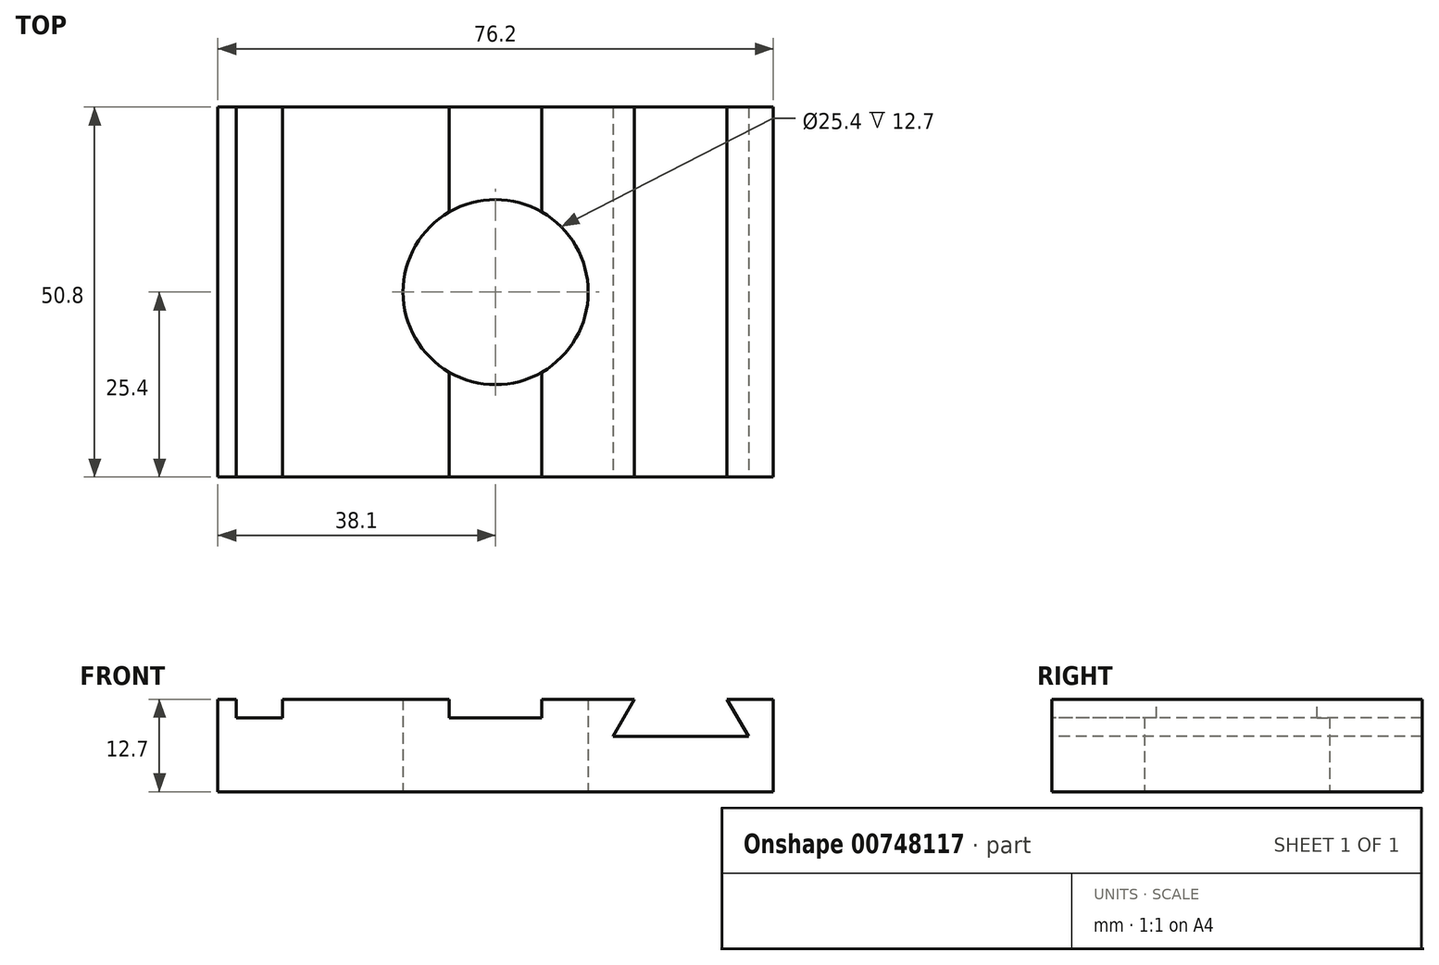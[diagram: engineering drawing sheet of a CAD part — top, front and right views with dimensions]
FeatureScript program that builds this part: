
annotation { "Feature Type Name" : "Feature", "Feature Type Description" : "" }
export const myFeature = defineFeature(function(context is Context, id is Id, definition is map)
    precondition{}
    {
        {
            var Q0;
            Q0=qCreatedBy(makeId("Top.planeOp"),FACE);
            var sketch = newSketch(context, id + "F0", { "sketchPlane" : qUnion([Q0])});
            skLineSegment(sketch, "E0.bottom", {"start": v(38.1, -25.4) * mm, "end": v(-38.1, -25.4) * mm});
            skLineSegment(sketch, "E0.top", {"start": v(38.1, 25.4) * mm, "end": v(-38.1, 25.4) * mm});
            skLineSegment(sketch, "E0.left", {"start": v(38.1, -25.4) * mm, "end": v(38.1, 25.4) * mm});
            skLineSegment(sketch, "E0.right", {"start": v(-38.1, -25.4) * mm, "end": v(-38.1, 25.4) * mm});
            skPoint(sketch, "E0.middle", {"position": v(0, 0) * mm});
            skCircle(sketch, "E1", {"center": v(0, 0) * mm, "radius": 12.7 * mm});
            skSolve(sketch);
        }
        {
            var Q0;
            Q0=makeQuery(id+"F0.imprint","IMPRINT",FACE,{"disambiguationData":[TD([[makeQuery(id+"F0.imprint","IMPRINT",EDGE,{"derivedFrom":sQuery(id+"F0.wireOp",EDGE,"E0.bottom")}),-1.0]])]});
            extrude(context, id + "F1", {"entities" : qUnion([Q0]), "depth" : 12.7 * mm, "offsetDistance" : 25.4 * mm});
        }
        {
            var Q0;
            Q0=makeQuery(id+"F1.opExtrude","CAP_FACE",FACE,{"disambiguationData":[OSD([sQuery(id+"F0.wireOp",EDGE,"E0.bottom"),sQuery(id+"F0.wireOp",EDGE,"E0.top"),sQuery(id+"F0.wireOp",EDGE,"E0.left"),sQuery(id+"F0.wireOp",EDGE,"E0.right"),sQuery(id+"F0.wireOp",EDGE,"E1")])],"isStart":false});
            var sketch = newSketch(context, id + "F2", { "sketchPlane" : qUnion([Q0])});
            skLineSegment(sketch, "E2.bottom", {"start": v(-35.56, 25.4) * mm, "end": v(-29.21, 25.4) * mm});
            skLineSegment(sketch, "E2.top", {"start": v(-35.56, -25.4) * mm, "end": v(-29.21, -25.4) * mm});
            skLineSegment(sketch, "E2.left", {"start": v(-35.56, 25.4) * mm, "end": v(-35.56, -25.4) * mm});
            skLineSegment(sketch, "E2.right", {"start": v(-29.21, 25.4) * mm, "end": v(-29.21, -25.4) * mm});
            skLineSegment(sketch, "E3", {"start": v(-6.35, 25.4) * mm, "end": v(-6.35, -25.4) * mm});
            skLineSegment(sketch, "E4", {"start": v(-6.35, -25.4) * mm, "end": v(6.35, -25.4) * mm});
            skLineSegment(sketch, "E5", {"start": v(6.35, -25.4) * mm, "end": v(6.35, 25.4) * mm});
            skLineSegment(sketch, "E6", {"start": v(6.35, 25.4) * mm, "end": v(-6.35, 25.4) * mm});
            skPoint(sketch, "E7", {"position": v(0, 0) * mm});
            skPoint(sketch, "E8", {"position": v(0, 25.4) * mm});
            skLineSegment(sketch, "E9", {"start": v(0, 25.4) * mm, "end": v(0, -25.4) * mm, "construction": true});
            skSolve(sketch);
        }
        {
            var Q0;
            Q0=makeQuery(id+"F2.imprint","IMPRINT",FACE,{"disambiguationData":[TD([[makeQuery(id+"F2.imprint","IMPRINT",EDGE,{"derivedFrom":sQuery(id+"F2.wireOp",EDGE,"E2.bottom")}),1.0]])]});
            var Q1;
            {var subQ0=sQuery(id+"F2.wireOp",EDGE,"E6");Q1=makeQuery(id+"F2.imprint","IMPRINT",FACE,{"disambiguationData":[TD([[makeQuery(id+"F2.imprint","IMPRINT",EDGE,{"derivedFrom":subQ0}),1.0]])]});}
            var Q2;
            {var subQ0=sQuery(id+"F2.wireOp",EDGE,"E4");Q2=makeQuery(id+"F2.imprint","IMPRINT",FACE,{"disambiguationData":[TD([[makeQuery(id+"F2.imprint","IMPRINT",EDGE,{"derivedFrom":subQ0}),-1.0]])]});}
            extrude(context, id + "F3", {"entities" : qUnion([Q0, Q1, Q2]), "operationType" : NewBodyOperationType.REMOVE, "oppositeDirection" : true, "depth" : 2.54 * mm, "offsetDistance" : 25.4 * mm});
        }
        {
            var Q0;
            Q0=makeQuery(id+"F1.opExtrude","SWEPT_FACE",FACE,{"disambiguationData":[OSD([sQuery(id+"F0.wireOp",EDGE,"E0.bottom")])]});
            var sketch = newSketch(context, id + "F4", { "sketchPlane" : qUnion([Q0])});
            skLineSegment(sketch, "E10", {"start": v(19.05, 12.7) * mm, "end": v(16.12, 7.62) * mm});
            skLineSegment(sketch, "E11", {"start": v(16.12, 7.62) * mm, "end": v(34.68, 7.62) * mm});
            skLineSegment(sketch, "E12", {"start": v(34.68, 7.62) * mm, "end": v(31.75, 12.7) * mm});
            skLineSegment(sketch, "E13", {"start": v(25.4, 7.62) * mm, "end": v(25.4, 12.7) * mm, "construction": true});
            skPoint(sketch, "E13.endSnap0", {"position": v(22.23, 12.7) * mm});
            skSolve(sketch);
        }
        {
            var Q0;
            {var subQ0=sQuery(id+"F4.wireOp",EDGE,"E10");Q0=makeQuery(id+"F4.imprint","IMPRINT",FACE,{"disambiguationData":[TD([[makeQuery(id+"F4.imprint","IMPRINT",EDGE,{"derivedFrom":subQ0}),1.0]])]});}
            extrude(context, id + "F5", {"entities" : qUnion([Q0]), "operationType" : NewBodyOperationType.REMOVE, "endBound" : BoundingType.THROUGH_ALL, "oppositeDirection" : true, "depth" : 25.4 * mm, "offsetDistance" : 25.4 * mm});
        }
    });
